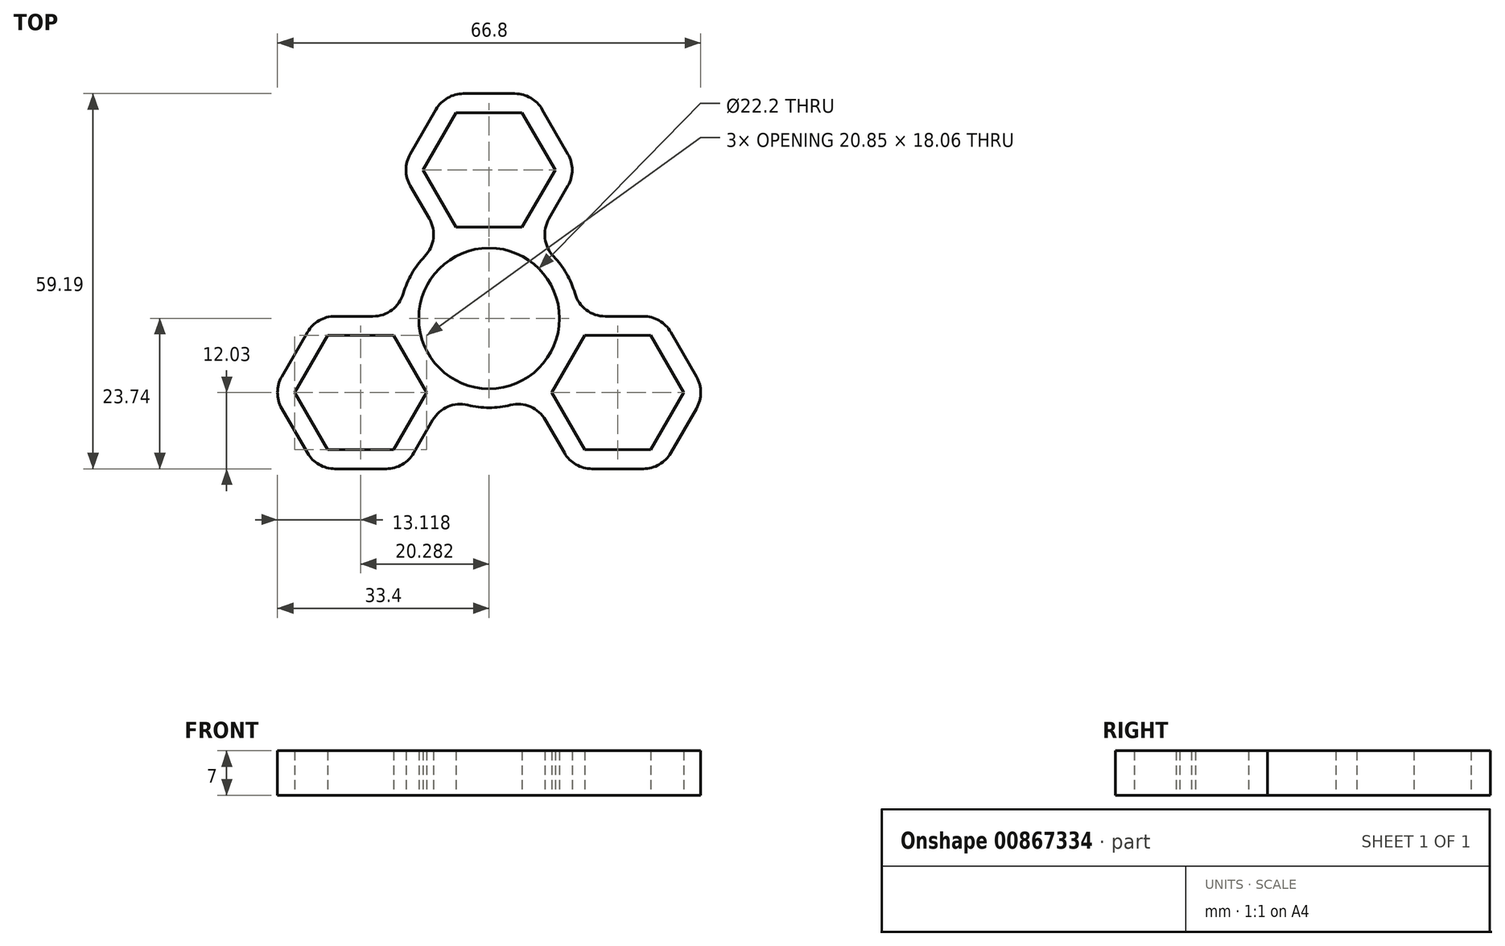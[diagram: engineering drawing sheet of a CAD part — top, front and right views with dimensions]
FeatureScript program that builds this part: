
annotation { "Feature Type Name" : "Feature", "Feature Type Description" : "" }
export const myFeature = defineFeature(function(context is Context, id is Id, definition is map)
    precondition{}
    {
        {
            var Q0;
            Q0=qCreatedBy(makeId("Top.planeOp"),FACE);
            var sketch = newSketch(context, id + "F0", { "sketchPlane" : qUnion([Q0])});
            skCircle(sketch, "E0", {"center": v(0, 0) * mm, "radius": 11.1 * mm});
            skLineSegment(sketch, "E1.0", {"start": v(-5.21, 32.45) * mm, "end": v(5.21, 32.45) * mm});
            skLineSegment(sketch, "E1.1", {"start": v(5.21, 32.45) * mm, "end": v(10.43, 23.42) * mm});
            skLineSegment(sketch, "E1.2", {"start": v(10.43, 23.42) * mm, "end": v(5.21, 14.4) * mm});
            skLineSegment(sketch, "E1.3", {"start": v(5.21, 14.4) * mm, "end": v(-5.21, 14.4) * mm});
            skLineSegment(sketch, "E1.4", {"start": v(-5.21, 14.4) * mm, "end": v(-10.43, 23.42) * mm});
            skLineSegment(sketch, "E1.5", {"start": v(-10.43, 23.42) * mm, "end": v(-5.21, 32.45) * mm});
            skPoint(sketch, "E1.0.midPoint", {"position": v(0, 32.45) * mm});
            skLineSegment(sketch, "E2.0", {"start": v(-4.06, 35.45) * mm, "end": v(4.06, 35.45) * mm});
            skLineSegment(sketch, "E2.1", {"start": v(8.39, 32.95) * mm, "end": v(12.45, 25.92) * mm});
            skLineSegment(sketch, "E2.2", {"start": v(12.45, 20.92) * mm, "end": v(9.45, 15.73) * mm});
            skLineSegment(sketch, "E2.4", {"start": v(-9.45, 15.73) * mm, "end": v(-12.45, 20.92) * mm});
            skLineSegment(sketch, "E2.5", {"start": v(-12.45, 25.92) * mm, "end": v(-8.39, 32.95) * mm});
            skPoint(sketch, "E2.0.midPoint", {"position": v(0, 35.45) * mm});
            skLineSegment(sketch, "E3.1.0", {"start": v(-25.5, -2.68) * mm, "end": v(-15.07, -2.68) * mm});
            skLineSegment(sketch, "E3.1.1", {"start": v(-9.86, -11.7) * mm, "end": v(-15.07, -20.74) * mm});
            skLineSegment(sketch, "E3.1.2", {"start": v(-15.07, -20.74) * mm, "end": v(-25.5, -20.74) * mm});
            skLineSegment(sketch, "E3.1.3", {"start": v(-16.22, -23.74) * mm, "end": v(-24.34, -23.74) * mm});
            skLineSegment(sketch, "E3.1.4", {"start": v(-24.34, 0.32) * mm, "end": v(-18.34, 0.32) * mm});
            skLineSegment(sketch, "E3.1.5", {"start": v(-15.07, -2.68) * mm, "end": v(-9.86, -11.7) * mm});
            skLineSegment(sketch, "E3.1.6", {"start": v(-28.67, -21.24) * mm, "end": v(-32.73, -14.2) * mm});
            skLineSegment(sketch, "E3.1.7", {"start": v(-30.7, -11.71) * mm, "end": v(-25.5, -2.68) * mm});
            skLineSegment(sketch, "E3.1.8", {"start": v(-32.73, -9.2) * mm, "end": v(-28.67, -2.18) * mm});
            skPoint(sketch, "E3.1.9", {"position": v(-30.7, -17.72) * mm});
            skLineSegment(sketch, "E3.1.10", {"start": v(-8.9, -16.05) * mm, "end": v(-11.9, -21.24) * mm});
            skLineSegment(sketch, "E3.1.11", {"start": v(-25.5, -20.74) * mm, "end": v(-30.7, -11.7) * mm});
            skPoint(sketch, "E3.1.12", {"position": v(-28.1, -16.22) * mm});
            skLineSegment(sketch, "E3.2.0", {"start": v(15.07, -20.74) * mm, "end": v(9.86, -11.71) * mm});
            skLineSegment(sketch, "E3.2.1", {"start": v(15.07, -2.68) * mm, "end": v(25.5, -2.68) * mm});
            skLineSegment(sketch, "E3.2.2", {"start": v(25.5, -2.68) * mm, "end": v(30.7, -11.71) * mm});
            skLineSegment(sketch, "E3.2.3", {"start": v(28.67, -2.18) * mm, "end": v(32.73, -9.21) * mm});
            skLineSegment(sketch, "E3.2.4", {"start": v(11.9, -21.24) * mm, "end": v(8.9, -16.05) * mm});
            skLineSegment(sketch, "E3.2.5", {"start": v(9.86, -11.71) * mm, "end": v(15.07, -2.68) * mm});
            skLineSegment(sketch, "E3.2.6", {"start": v(32.73, -14.21) * mm, "end": v(28.67, -21.24) * mm});
            skLineSegment(sketch, "E3.2.7", {"start": v(25.5, -20.74) * mm, "end": v(15.07, -20.74) * mm});
            skLineSegment(sketch, "E3.2.8", {"start": v(24.34, -23.74) * mm, "end": v(16.22, -23.74) * mm});
            skPoint(sketch, "E3.2.9", {"position": v(30.7, -17.73) * mm});
            skLineSegment(sketch, "E3.2.10", {"start": v(18.34, 0.32) * mm, "end": v(24.34, 0.32) * mm});
            skLineSegment(sketch, "E3.2.11", {"start": v(30.7, -11.71) * mm, "end": v(25.5, -20.74) * mm});
            skPoint(sketch, "E3.2.12", {"position": v(28.1, -16.23) * mm});
            skArc(sketch, "E4.0", {"start": v(-10.17, 9.76) * mm, "mid": v(-12.21, 7.05) * mm, "end": v(-13.54, 3.93) * mm});
            skArc(sketch, "E5.trimOffspring", {"start": v(13.54, 3.93) * mm, "mid": v(12.21, 7.05) * mm, "end": v(10.17, 9.76) * mm});
            skArc(sketch, "E6.trimOffspring", {"start": v(-3.37, -13.7) * mm, "mid": v(0, -14.1) * mm, "end": v(3.37, -13.7) * mm});
            skPoint(sketch, "E7.newPointA", {"position": v(-6.95, 11.4) * mm});
            skArc(sketch, "E7.filletArc", {"start": v(-10.17, 9.76) * mm, "mid": v(-8.82, 12.62) * mm, "end": v(-9.45, 15.73) * mm});
            skPoint(sketch, "E8.newPointB", {"position": v(-13.34, 0.32) * mm});
            skArc(sketch, "E8.filletArc", {"start": v(-18.34, 0.32) * mm, "mid": v(-15.34, 1.32) * mm, "end": v(-13.54, 3.93) * mm});
            skPoint(sketch, "E9.newPointA", {"position": v(-6.4, -11.7) * mm});
            skArc(sketch, "E9.filletArc", {"start": v(-3.37, -13.7) * mm, "mid": v(-6.53, -13.95) * mm, "end": v(-8.9, -16.05) * mm});
            skPoint(sketch, "E10.newPointB", {"position": v(6.4, -11.7) * mm});
            skArc(sketch, "E10.filletArc", {"start": v(8.9, -16.05) * mm, "mid": v(6.53, -13.95) * mm, "end": v(3.37, -13.7) * mm});
            skPoint(sketch, "E11.newPointA", {"position": v(13.34, 0.32) * mm});
            skArc(sketch, "E11.filletArc", {"start": v(13.54, 3.93) * mm, "mid": v(15.34, 1.32) * mm, "end": v(18.34, 0.32) * mm});
            skPoint(sketch, "E12.newPointB", {"position": v(6.95, 11.4) * mm});
            skArc(sketch, "E12.filletArc", {"start": v(9.45, 15.73) * mm, "mid": v(8.82, 12.62) * mm, "end": v(10.17, 9.76) * mm});
            skPoint(sketch, "E13.visualSharp", {"position": v(13.9, 23.42) * mm});
            skArc(sketch, "E13.filletArc", {"start": v(12.45, 20.92) * mm, "mid": v(13.12, 23.42) * mm, "end": v(12.45, 25.92) * mm});
            skPoint(sketch, "E14.visualSharp", {"position": v(6.95, 35.45) * mm});
            skArc(sketch, "E14.filletArc", {"start": v(8.39, 32.95) * mm, "mid": v(6.56, 34.78) * mm, "end": v(4.06, 35.45) * mm});
            skPoint(sketch, "E15.visualSharp", {"position": v(-6.95, 35.45) * mm});
            skArc(sketch, "E15.filletArc", {"start": v(-4.06, 35.45) * mm, "mid": v(-6.56, 34.78) * mm, "end": v(-8.39, 32.95) * mm});
            skPoint(sketch, "E16.visualSharp", {"position": v(-13.9, 23.42) * mm});
            skArc(sketch, "E16.filletArc", {"start": v(-12.45, 25.92) * mm, "mid": v(-13.12, 23.42) * mm, "end": v(-12.45, 20.92) * mm});
            skPoint(sketch, "E17.visualSharp", {"position": v(-27.23, 0.32) * mm});
            skArc(sketch, "E17.filletArc", {"start": v(-24.34, 0.32) * mm, "mid": v(-26.84, -0.35) * mm, "end": v(-28.67, -2.18) * mm});
            skPoint(sketch, "E18.visualSharp", {"position": v(-34.17, -11.7) * mm});
            skArc(sketch, "E18.filletArc", {"start": v(-32.73, -9.2) * mm, "mid": v(-33.4, -11.7) * mm, "end": v(-32.73, -14.2) * mm});
            skPoint(sketch, "E19.visualSharp", {"position": v(27.23, 0.32) * mm});
            skArc(sketch, "E19.filletArc", {"start": v(28.67, -2.18) * mm, "mid": v(26.84, -0.35) * mm, "end": v(24.34, 0.32) * mm});
            skPoint(sketch, "E20.visualSharp", {"position": v(34.17, -11.71) * mm});
            skArc(sketch, "E20.filletArc", {"start": v(32.73, -14.21) * mm, "mid": v(33.4, -11.71) * mm, "end": v(32.73, -9.21) * mm});
            skPoint(sketch, "E21.visualSharp", {"position": v(27.23, -23.74) * mm});
            skArc(sketch, "E21.filletArc", {"start": v(24.34, -23.74) * mm, "mid": v(26.84, -23.07) * mm, "end": v(28.67, -21.24) * mm});
            skPoint(sketch, "E22.visualSharp", {"position": v(13.34, -23.74) * mm});
            skArc(sketch, "E22.filletArc", {"start": v(11.9, -21.24) * mm, "mid": v(13.72, -23.07) * mm, "end": v(16.22, -23.74) * mm});
            skPoint(sketch, "E23.visualSharp", {"position": v(-13.34, -23.74) * mm});
            skArc(sketch, "E23.filletArc", {"start": v(-16.22, -23.74) * mm, "mid": v(-13.72, -23.07) * mm, "end": v(-11.9, -21.24) * mm});
            skPoint(sketch, "E24.visualSharp", {"position": v(-27.23, -23.74) * mm});
            skArc(sketch, "E24.filletArc", {"start": v(-28.67, -21.24) * mm, "mid": v(-26.84, -23.07) * mm, "end": v(-24.34, -23.74) * mm});
            skSolve(sketch);
        }
        {
            var Q0;
            Q0 = qSketchRegion(id + "F0", true);
            extrude(context, id + "F1", {"entities" : qUnion([Q0]), "depth" : 7 * mm, "offsetDistance" : 25 * mm});
        }
    });
